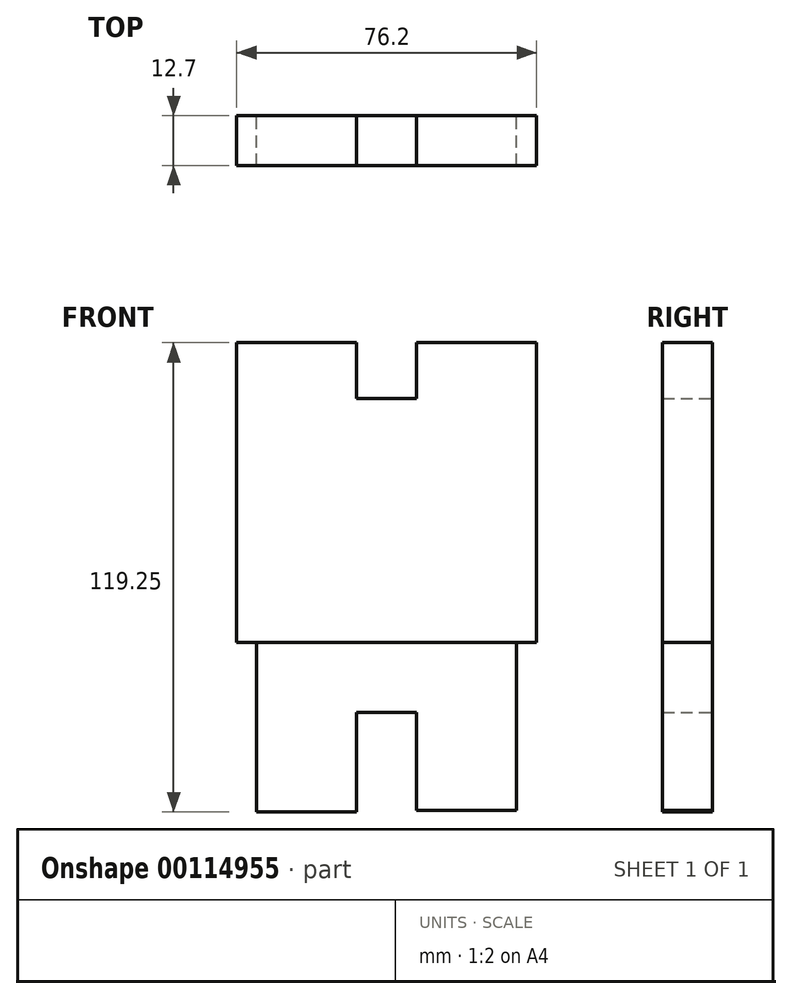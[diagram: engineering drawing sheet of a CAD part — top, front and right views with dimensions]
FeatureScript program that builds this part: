
annotation { "Feature Type Name" : "Feature", "Feature Type Description" : "" }
export const myFeature = defineFeature(function(context is Context, id is Id, definition is map)
    precondition{}
    {
        {
            var Q0;
            Q0=qCreatedBy(makeId("Front.planeOp"),FACE);
            var sketch = newSketch(context, id + "F0", { "sketchPlane" : qUnion([Q0])});
            skLineSegment(sketch, "E0", {"start": v(0, 0) * mm, "end": v(0, -76.2) * mm});
            skLineSegment(sketch, "E1", {"start": v(0, -76.2) * mm, "end": v(76.2, -76.2) * mm});
            skLineSegment(sketch, "E2", {"start": v(76.2, -76.2) * mm, "end": v(76.2, 0) * mm});
            skLineSegment(sketch, "E3", {"start": v(76.2, 0) * mm, "end": v(0, 0) * mm});
            skSolve(sketch);
        }
        {
            var Q0;
            Q0=makeQuery(id+"F0.imprint","IMPRINT",FACE,{"disambiguationData":[TD([[makeQuery(id+"F0.imprint","IMPRINT",EDGE,{"derivedFrom":sQuery(id+"F0.wireOp",EDGE,"E0")}),1.0]])]});
            extrude(context, id + "F1", {"entities" : qUnion([Q0]), "depth" : 12.7 * mm});
        }
        {
            var Q0;
            Q0=qCreatedBy(makeId("Front.planeOp"),FACE);
            var sketch = newSketch(context, id + "F2", { "sketchPlane" : qUnion([Q0])});
            skLineSegment(sketch, "E4", {"start": v(30.48, 0) * mm, "end": v(30.48, -14.22) * mm});
            skLineSegment(sketch, "E5", {"start": v(30.48, -14.22) * mm, "end": v(45.72, -14.22) * mm});
            skLineSegment(sketch, "E6", {"start": v(45.72, -14.22) * mm, "end": v(45.72, 0) * mm});
            skLineSegment(sketch, "E7", {"start": v(45.72, 0) * mm, "end": v(30.48, 0) * mm});
            skSolve(sketch);
        }
        {
            var Q0;
            Q0=makeQuery(id+"F2.imprint","IMPRINT",FACE,{"disambiguationData":[TD([[makeQuery(id+"F2.imprint","IMPRINT",EDGE,{"derivedFrom":sQuery(id+"F2.wireOp",EDGE,"E4")}),1.0]])]});
            extrude(context, id + "F3", {"entities" : qUnion([Q0]), "operationType" : NewBodyOperationType.REMOVE, "depth" : 25.4 * mm});
        }
        {
            var Q0;
            Q0=makeQuery(id+"F1.opExtrude","CAP_FACE",FACE,{"disambiguationData":[OSD([sQuery(id+"F0.wireOp",EDGE,"E0"),sQuery(id+"F0.wireOp",EDGE,"E1"),sQuery(id+"F0.wireOp",EDGE,"E2"),sQuery(id+"F0.wireOp",EDGE,"E3")])],"isStart":true});
            var sketch = newSketch(context, id + "F4", { "sketchPlane" : qUnion([Q0])});
            skLineSegment(sketch, "E8", {"start": v(-71.12, -76.2) * mm, "end": v(-71.12, -118.86) * mm});
            skLineSegment(sketch, "E9", {"start": v(-71.12, -118.86) * mm, "end": v(-45.72, -118.86) * mm});
            skLineSegment(sketch, "E10", {"start": v(-45.72, -118.86) * mm, "end": v(-45.72, -93.98) * mm});
            skLineSegment(sketch, "E11", {"start": v(-45.72, -93.98) * mm, "end": v(-30.48, -93.98) * mm});
            skLineSegment(sketch, "E12", {"start": v(-30.48, -93.98) * mm, "end": v(-30.48, -119.25) * mm});
            skLineSegment(sketch, "E13", {"start": v(-30.48, -119.25) * mm, "end": v(-5.08, -119.25) * mm});
            skLineSegment(sketch, "E14", {"start": v(-5.08, -119.25) * mm, "end": v(-5.08, -76.2) * mm});
            skSolve(sketch);
        }
        {
            var Q0;
            {var subQ1=sQuery(id+"F4.wireOp",EDGE,"E8");Q0=makeQuery(id+"F4.imprint","IMPRINT",FACE,{"disambiguationData":[TD([[makeQuery(id+"F4.imprint","IMPRINT",EDGE,{"derivedFrom":subQ1}),1.0]])]});}
            extrude(context, id + "F5", {"entities" : qUnion([Q0]), "oppositeDirection" : true, "depth" : 12.7 * mm});
        }
    });
